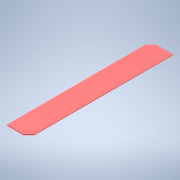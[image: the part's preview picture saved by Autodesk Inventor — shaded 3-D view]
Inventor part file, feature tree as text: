
AUTODESK INVENTOR PART (.ipt)
format: ipt  version: 2021 (Build 250183000, 183)  size: 99,328 bytes
history: native  units: mm
features: extrude x1, sketch x1
ambient origin geometry x8: Origin, YZ Plane, XZ Plane, XY Plane, X Axis, Y Axis, Z Axis, Center Point
bodies: Solid1 (feature_tree)
feature tree (2):
  extrude  "Extrusion1"  Depth=251.0mm
  sketch  "Sketch1"  dims[d0=38.0mm d1=251.0mm d2=10.0mm d3=10.0mm d4=1.7mm d5=0.0mm]
